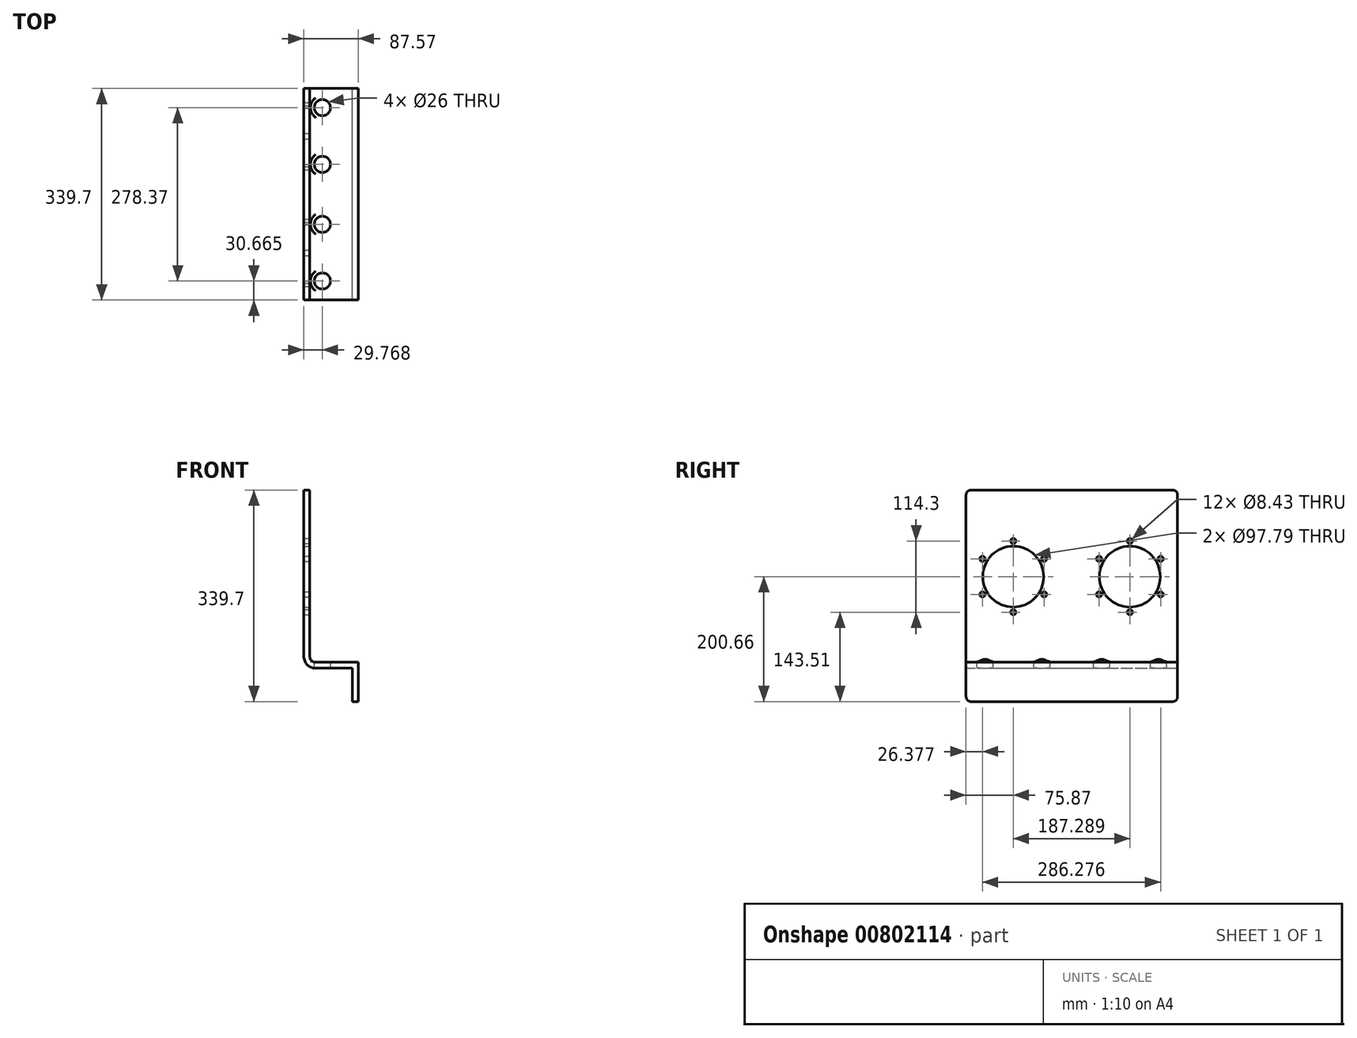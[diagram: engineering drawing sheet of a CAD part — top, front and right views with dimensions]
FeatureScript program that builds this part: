
annotation { "Feature Type Name" : "Feature", "Feature Type Description" : "" }
export const myFeature = defineFeature(function(context is Context, id is Id, definition is map)
    precondition{}
    {
        {
            var Q0;
            Q0=qCreatedBy(makeId("Front.planeOp"),FACE);
            var sketch = newSketch(context, id + "F0", { "sketchPlane" : qUnion([Q0])});
            skLineSegment(sketch, "E0", {"start": v(0, 0) * mm, "end": v(0, -267.17) * mm});
            skLineSegment(sketch, "E1", {"start": v(9.53, -276.7) * mm, "end": v(78.04, -276.7) * mm});
            skLineSegment(sketch, "E2", {"start": v(0, 0) * mm, "end": v(-9.52, 0) * mm});
            skLineSegment(sketch, "E3", {"start": v(-9.52, 0) * mm, "end": v(-9.52, -267.17) * mm});
            skLineSegment(sketch, "E4", {"start": v(9.53, -286.22) * mm, "end": v(68.51, -286.22) * mm});
            skLineSegment(sketch, "E5", {"start": v(78.04, -276.7) * mm, "end": v(78.04, -339.7) * mm});
            skLineSegment(sketch, "E6", {"start": v(68.51, -286.22) * mm, "end": v(68.51, -339.7) * mm});
            skLineSegment(sketch, "E7", {"start": v(68.51, -339.7) * mm, "end": v(78.04, -339.7) * mm});
            skPoint(sketch, "E8.visualSharp", {"position": v(0, -276.7) * mm});
            skArc(sketch, "E8.filletArc", {"start": v(0, -267.17) * mm, "mid": v(2.79, -273.9) * mm, "end": v(9.53, -276.7) * mm});
            skPoint(sketch, "E9.visualSharp", {"position": v(-9.52, -286.22) * mm});
            skArc(sketch, "E9.filletArc", {"start": v(-9.52, -267.17) * mm, "mid": v(-3.95, -280.64) * mm, "end": v(9.53, -286.22) * mm});
            skSolve(sketch);
        }
        {
            var Q0;
            Q0=qSketchRegion(id+"F0",true);
            extrude(context, id + "F1", {"entities" : qUnion([Q0]), "depth" : 339.7 * mm, "offsetDistance" : 25 * mm});
        }
        {
            var Q0;
            Q0=makeQuery(id+"F1.opExtrude","CAP_EDGE",EDGE,{"disambiguationData":[OSD([sQuery(id+"F0.wireOp",EDGE,"E2")])],"isStart":false});
            fillet(context, id + "F2", {"entities" : qUnion([Q0]), "radius" : 7.95 * mm, "tangentPropagation" : true, "allowEdgeOverflow" : false});
        }
        {
            var Q0;
            Q0=makeQuery(id+"F1.opExtrude","CAP_EDGE",EDGE,{"disambiguationData":[OSD([sQuery(id+"F0.wireOp",EDGE,"E2")])],"isStart":true});
            var Q1;
            Q1=makeQuery(id+"F1.opExtrude","CAP_EDGE",EDGE,{"disambiguationData":[OSD([sQuery(id+"F0.wireOp",EDGE,"E7")])],"isStart":true});
            var Q2;
            Q2=makeQuery(id+"F1.opExtrude","CAP_EDGE",EDGE,{"disambiguationData":[OSD([sQuery(id+"F0.wireOp",EDGE,"E7")])],"isStart":false});
            fillet(context, id + "F3", {"entities" : qUnion([Q0, Q1, Q2]), "radius" : 7.95 * mm, "tangentPropagation" : true, "allowEdgeOverflow" : false});
        }
        {
            var Q0;
            Q0=makeQuery(id+"F1.opExtrude","SWEPT_FACE",FACE,{"disambiguationData":[OSD([sQuery(id+"F0.wireOp",EDGE,"E0")])]});
            var sketch = newSketch(context, id + "F4", { "sketchPlane" : qUnion([Q0])});
            skPoint(sketch, "E10", {"position": v(-263.83, -139.04) * mm});
            skPoint(sketch, "E11", {"position": v(-76.54, -139.04) * mm});
            skCircle(sketch, "E12", {"center": v(-76.54, -139.04) * mm, "radius": 48.9 * mm});
            skCircle(sketch, "E13", {"center": v(-263.83, -139.04) * mm, "radius": 48.9 * mm});
            skPoint(sketch, "E14", {"position": v(-263.83, -81.89) * mm});
            skPoint(sketch, "E15", {"position": v(-76.54, -81.89) * mm});
            skPoint(sketch, "E16.1.0", {"position": v(-126.03, -110.46) * mm});
            skPoint(sketch, "E16.2.0", {"position": v(-126.03, -167.61) * mm});
            skPoint(sketch, "E16.3.0", {"position": v(-76.54, -196.2) * mm});
            skPoint(sketch, "E16.4.0", {"position": v(-27.05, -167.62) * mm});
            skPoint(sketch, "E16.5.0", {"position": v(-27.05, -110.47) * mm});
            skPoint(sketch, "E17.1.0", {"position": v(-313.32, -110.46) * mm});
            skPoint(sketch, "E17.2.0", {"position": v(-313.32, -167.61) * mm});
            skPoint(sketch, "E17.3.0", {"position": v(-263.83, -196.2) * mm});
            skPoint(sketch, "E17.4.0", {"position": v(-214.34, -167.62) * mm});
            skPoint(sketch, "E17.5.0", {"position": v(-214.34, -110.47) * mm});
            skSolve(sketch);
        }
        {
            var Q0;
            Q0=qSketchRegion(id+"F4",true);
            extrude(context, id + "F5", {"entities" : qUnion([Q0]), "operationType" : NewBodyOperationType.REMOVE, "endBound" : BoundingType.THROUGH_ALL, "oppositeDirection" : true, "depth" : 25 * mm});
        }
        {
            var Q0;
            Q0=sQuery(id+"F4.wireOp",VERTEX,"E14");
            var Q1;
            Q1=sQuery(id+"F4.wireOp",VERTEX,"E17.1.0");
            var Q2;
            Q2=sQuery(id+"F4.wireOp",VERTEX,"E17.2.0");
            var Q3;
            Q3=sQuery(id+"F4.wireOp",VERTEX,"E17.3.0");
            var Q4;
            Q4=sQuery(id+"F4.wireOp",VERTEX,"E17.4.0");
            var Q5;
            Q5=sQuery(id+"F4.wireOp",VERTEX,"E17.5.0");
            var Q6;
            Q6=sQuery(id+"F4.wireOp",VERTEX,"E16.1.0");
            var Q7;
            Q7=sQuery(id+"F4.wireOp",VERTEX,"E15");
            var Q8;
            Q8=sQuery(id+"F4.wireOp",VERTEX,"E16.5.0");
            var Q9;
            Q9=sQuery(id+"F4.wireOp",VERTEX,"E16.4.0");
            var Q10;
            Q10=sQuery(id+"F4.wireOp",VERTEX,"E16.3.0");
            var Q11;
            Q11=sQuery(id+"F4.wireOp",VERTEX,"E16.2.0");
            var Q12;
            Q12=makeQuery(id+"F1.opExtrude","SWEPT_BODY",BODY,{"disambiguationData":[OSD([sQuery(id+"F0.wireOp",EDGE,"E0"),sQuery(id+"F0.wireOp",EDGE,"E1"),sQuery(id+"F0.wireOp",EDGE,"E2"),sQuery(id+"F0.wireOp",EDGE,"E3"),sQuery(id+"F0.wireOp",EDGE,"E4"),sQuery(id+"F0.wireOp",EDGE,"E5"),sQuery(id+"F0.wireOp",EDGE,"E6"),sQuery(id+"F0.wireOp",EDGE,"E7"),sQuery(id+"F0.wireOp",EDGE,"E8.filletArc"),sQuery(id+"F0.wireOp",EDGE,"E9.filletArc")])]});
            hole(context, id + "F6", {"style" : HoleStyle.SIMPLE, "endStyle" : HoleEndStyle.THROUGH, "standardTappedOrClearance" : lookupTablePath({ "standard" : "ANSI", "fit" : "Normal (ASME)", "size" : "5/16", "type" : "Clearance" }), "standardBlindInLast" : lookupTablePath({ "fit" : "Free", "standard" : "ANSI", "size" : "5/16", "type" : "Clearance" }), "holeDiameter" : 8.43 * mm, "tappedDepth" : 25 * mm, "tapClearance" : 3, "startFromSketch" : true, "locations" : qUnion([Q0, Q1, Q2, Q3, Q4, Q5, Q6, Q7, Q8, Q9, Q10, Q11]), "scope" : qUnion([Q12])});
        }
        {
            var Q0;
            Q0=makeQuery(id+"F1.opExtrude","SWEPT_FACE",FACE,{"disambiguationData":[OSD([sQuery(id+"F0.wireOp",EDGE,"E1")])]});
            var sketch = newSketch(context, id + "F7", { "sketchPlane" : qUnion([Q0])});
            skPoint(sketch, "E18", {"position": v(20.24, -30.67) * mm});
            skPoint(sketch, "E19", {"position": v(20.24, -121.75) * mm});
            skPoint(sketch, "E20", {"position": v(20.24, -217.96) * mm});
            skPoint(sketch, "E21", {"position": v(20.24, -309.04) * mm});
            skSolve(sketch);
        }
        {
            var Q0;
            Q0=sQuery(id+"F7.wireOp",VERTEX,"E18");
            var Q1;
            Q1=sQuery(id+"F7.wireOp",VERTEX,"E19");
            var Q2;
            Q2=sQuery(id+"F7.wireOp",VERTEX,"E20");
            var Q3;
            Q3=sQuery(id+"F7.wireOp",VERTEX,"E21");
            var Q4;
            Q4=makeQuery(id+"F1.opExtrude","SWEPT_BODY",BODY,{"disambiguationData":[OSD([sQuery(id+"F0.wireOp",EDGE,"E0"),sQuery(id+"F0.wireOp",EDGE,"E1"),sQuery(id+"F0.wireOp",EDGE,"E2"),sQuery(id+"F0.wireOp",EDGE,"E3"),sQuery(id+"F0.wireOp",EDGE,"E4"),sQuery(id+"F0.wireOp",EDGE,"E5"),sQuery(id+"F0.wireOp",EDGE,"E6"),sQuery(id+"F0.wireOp",EDGE,"E7"),sQuery(id+"F0.wireOp",EDGE,"E8.filletArc"),sQuery(id+"F0.wireOp",EDGE,"E9.filletArc")])]});
            hole(context, id + "F8", {"style" : HoleStyle.SIMPLE, "endStyle" : HoleEndStyle.THROUGH, "holeDiameter" : 26 * mm, "majorDiameter" : 5 * mm, "isTappedThrough" : true, "tappedDepth" : 17 * mm, "tapClearance" : 3, "startFromSketch" : true, "locations" : qUnion([Q0, Q1, Q2, Q3]), "scope" : qUnion([Q4])});
        }
        {
            var Q0;
            {var subQ0=sQuery(id+"F0.wireOp",EDGE,"E1");Q0=makeQuery(id+"F7.imprint","IMPRINT",FACE,{"disambiguationData":[TD([[makeQuery(id+"F7.imprint","IMPRINT",EDGE,{"derivedFrom":makeQuery(id+"F1.opExtrude","CAP_EDGE",EDGE,{"disambiguationData":[OSD([subQ0])],"isStart":true})}),-1.0]])]});}
            var sketch = newSketch(context, id + "F9", { "sketchPlane" : qUnion([Q0])});
            skCircle(sketch, "E22", {"center": v(20.24, -30.67) * mm, "radius": 19.05 * mm});
            skCircle(sketch, "E23", {"center": v(20.24, -121.75) * mm, "radius": 19.05 * mm});
            skCircle(sketch, "E24", {"center": v(20.24, -217.96) * mm, "radius": 19.05 * mm});
            skCircle(sketch, "E25", {"center": v(20.24, -309.04) * mm, "radius": 19.05 * mm});
            skSolve(sketch);
        }
        {
            var Q0;
            Q0=qSketchRegion(id+"F9",true);
            extrude(context, id + "F10", {"entities" : qUnion([Q0]), "operationType" : NewBodyOperationType.REMOVE, "depth" : 25 * mm, "offsetDistance" : 25 * mm});
        }
    });
